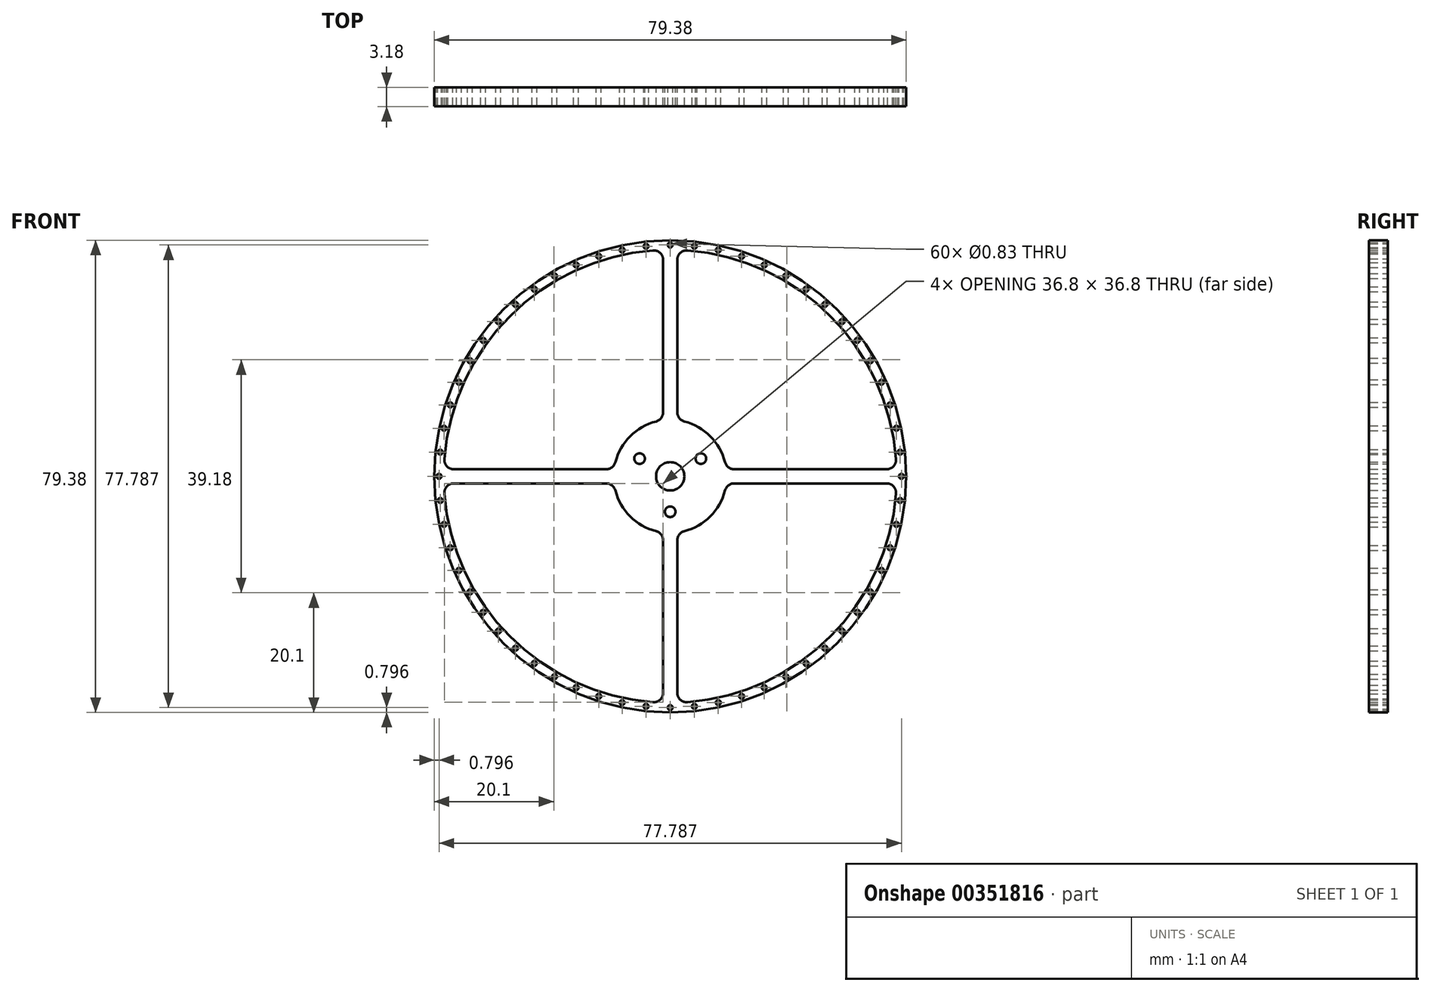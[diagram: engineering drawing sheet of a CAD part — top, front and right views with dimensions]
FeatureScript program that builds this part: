
annotation { "Feature Type Name" : "Feature", "Feature Type Description" : "" }
export const myFeature = defineFeature(function(context is Context, id is Id, definition is map)
    precondition{}
    {
        {
            var Q0;
            Q0=qCreatedBy(makeId("Front.planeOp"),FACE);
            var sketch = newSketch(context, id + "F0", { "sketchPlane" : qUnion([Q0])});
            skCircle(sketch, "E0", {"center": v(0, 0) * mm, "radius": 39.69 * mm});
            skArc(sketch, "E1", {"start": v(-0.98, 38.88) * mm, "mid": v(0.93, -38.88) * mm, "end": v(-0.88, 38.88) * mm, "construction": true});
            skArc(sketch, "E2", {"start": v(-2.9, 37.99) * mm, "mid": v(-26.94, 26.94) * mm, "end": v(-37.99, 2.9) * mm});
            skArc(sketch, "E3", {"start": v(-2.38, 9.22) * mm, "mid": v(-6.74, 6.74) * mm, "end": v(-9.22, 2.38) * mm});
            skCircle(sketch, "E4", {"center": v(0, 0) * mm, "radius": 2.38 * mm});
            skLineSegment(sketch, "E5.trimOffspring", {"start": v(1.2, 36.4) * mm, "end": v(1.2, 10.76) * mm});
            skLineSegment(sketch, "E6.trimOffspring", {"start": v(-1.2, 36.4) * mm, "end": v(-1.2, 10.76) * mm});
            skLineSegment(sketch, "E7.1.0", {"start": v(-36.4, -1.2) * mm, "end": v(-10.76, -1.2) * mm});
            skLineSegment(sketch, "E7.1.1", {"start": v(-36.4, 1.2) * mm, "end": v(-10.76, 1.2) * mm});
            skLineSegment(sketch, "E7.2.0", {"start": v(1.2, -36.4) * mm, "end": v(1.2, -10.76) * mm});
            skLineSegment(sketch, "E7.2.1", {"start": v(-1.2, -36.4) * mm, "end": v(-1.2, -10.76) * mm});
            skLineSegment(sketch, "E7.3.0", {"start": v(36.4, 1.2) * mm, "end": v(10.76, 1.2) * mm});
            skLineSegment(sketch, "E7.3.1", {"start": v(36.4, -1.2) * mm, "end": v(10.76, -1.2) * mm});
            skArc(sketch, "E8.trimOffspring", {"start": v(-9.22, -2.38) * mm, "mid": v(-6.74, -6.74) * mm, "end": v(-2.38, -9.22) * mm});
            skArc(sketch, "E9.trimOffspring", {"start": v(2.38, -9.22) * mm, "mid": v(6.74, -6.74) * mm, "end": v(9.22, -2.38) * mm});
            skArc(sketch, "E10.trimOffspring", {"start": v(9.22, 2.38) * mm, "mid": v(6.74, 6.74) * mm, "end": v(2.38, 9.22) * mm});
            skArc(sketch, "E11.trimOffspring", {"start": v(-37.99, -2.9) * mm, "mid": v(-26.94, -26.94) * mm, "end": v(-2.9, -37.99) * mm});
            skArc(sketch, "E12.trimOffspring", {"start": v(37.99, 2.9) * mm, "mid": v(26.94, 26.94) * mm, "end": v(2.9, 37.99) * mm});
            skArc(sketch, "E13.trimOffspring", {"start": v(2.9, -37.99) * mm, "mid": v(26.94, -26.94) * mm, "end": v(37.99, -2.9) * mm});
            skCircle(sketch, "E14", {"center": v(0, 0) * mm, "radius": 5.95 * mm, "construction": true});
            skLineSegment(sketch, "E15", {"start": v(0, 0) * mm, "end": v(0, -12.7) * mm, "construction": true});
            skCircle(sketch, "E16", {"center": v(0, -5.95) * mm, "radius": 0.89 * mm});
            skCircle(sketch, "E17.1.0", {"center": v(5.16, 2.98) * mm, "radius": 0.89 * mm});
            skCircle(sketch, "E17.2.0", {"center": v(-5.16, 2.98) * mm, "radius": 0.89 * mm});
            skPoint(sketch, "E18.visualSharp", {"position": v(9.45, -1.2) * mm});
            skArc(sketch, "E18.filletArc", {"start": v(10.76, -1.2) * mm, "mid": v(9.79, -1.52) * mm, "end": v(9.22, -2.38) * mm});
            skPoint(sketch, "E19.visualSharp", {"position": v(9.45, 1.2) * mm});
            skArc(sketch, "E19.filletArc", {"start": v(9.22, 2.38) * mm, "mid": v(9.79, 1.52) * mm, "end": v(10.76, 1.2) * mm});
            skPoint(sketch, "E20.visualSharp", {"position": v(1.2, -9.45) * mm});
            skArc(sketch, "E20.filletArc", {"start": v(2.38, -9.22) * mm, "mid": v(1.52, -9.79) * mm, "end": v(1.2, -10.76) * mm});
            skPoint(sketch, "E21.visualSharp", {"position": v(-1.2, -9.45) * mm});
            skArc(sketch, "E21.filletArc", {"start": v(-1.2, -10.76) * mm, "mid": v(-1.52, -9.79) * mm, "end": v(-2.38, -9.22) * mm});
            skPoint(sketch, "E22.visualSharp", {"position": v(-9.45, -1.2) * mm});
            skArc(sketch, "E22.filletArc", {"start": v(-9.22, -2.38) * mm, "mid": v(-9.79, -1.52) * mm, "end": v(-10.76, -1.2) * mm});
            skPoint(sketch, "E23.visualSharp", {"position": v(-9.45, 1.2) * mm});
            skArc(sketch, "E23.filletArc", {"start": v(-10.76, 1.2) * mm, "mid": v(-9.79, 1.52) * mm, "end": v(-9.22, 2.38) * mm});
            skPoint(sketch, "E24.visualSharp", {"position": v(-1.2, 9.45) * mm});
            skArc(sketch, "E24.filletArc", {"start": v(-2.38, 9.22) * mm, "mid": v(-1.52, 9.79) * mm, "end": v(-1.2, 10.76) * mm});
            skPoint(sketch, "E25.visualSharp", {"position": v(1.2, 9.45) * mm});
            skArc(sketch, "E25.filletArc", {"start": v(1.2, 10.76) * mm, "mid": v(1.52, 9.79) * mm, "end": v(2.38, 9.22) * mm});
            skPoint(sketch, "E26.visualSharp", {"position": v(38.08, 1.2) * mm});
            skArc(sketch, "E26.filletArc", {"start": v(36.4, 1.2) * mm, "mid": v(37.57, 1.7) * mm, "end": v(37.99, 2.9) * mm});
            skPoint(sketch, "E27.visualSharp", {"position": v(38.08, -1.2) * mm});
            skArc(sketch, "E27.filletArc", {"start": v(37.99, -2.9) * mm, "mid": v(37.57, -1.7) * mm, "end": v(36.4, -1.2) * mm});
            skPoint(sketch, "E28.visualSharp", {"position": v(1.2, -38.08) * mm});
            skArc(sketch, "E28.filletArc", {"start": v(1.2, -36.4) * mm, "mid": v(1.7, -37.57) * mm, "end": v(2.9, -37.99) * mm});
            skPoint(sketch, "E29.visualSharp", {"position": v(-1.2, -38.08) * mm});
            skArc(sketch, "E29.filletArc", {"start": v(-2.9, -37.99) * mm, "mid": v(-1.7, -37.57) * mm, "end": v(-1.2, -36.4) * mm});
            skPoint(sketch, "E30.visualSharp", {"position": v(-38.08, -1.2) * mm});
            skArc(sketch, "E30.filletArc", {"start": v(-36.4, -1.2) * mm, "mid": v(-37.57, -1.7) * mm, "end": v(-37.99, -2.9) * mm});
            skPoint(sketch, "E31.visualSharp", {"position": v(-38.08, 1.2) * mm});
            skArc(sketch, "E31.filletArc", {"start": v(-37.99, 2.9) * mm, "mid": v(-37.57, 1.7) * mm, "end": v(-36.4, 1.2) * mm});
            skPoint(sketch, "E32.visualSharp", {"position": v(-1.2, 38.08) * mm});
            skArc(sketch, "E32.filletArc", {"start": v(-1.2, 36.4) * mm, "mid": v(-1.7, 37.57) * mm, "end": v(-2.9, 37.99) * mm});
            skPoint(sketch, "E33.visualSharp", {"position": v(1.2, 38.08) * mm});
            skArc(sketch, "E33.filletArc", {"start": v(2.9, 37.99) * mm, "mid": v(1.7, 37.57) * mm, "end": v(1.2, 36.4) * mm});
            skLineSegment(sketch, "E34", {"start": v(0, 0) * mm, "end": v(-43.18, 0) * mm, "construction": true});
            skCircle(sketch, "E35", {"center": v(-38.9, 0) * mm, "radius": 0.41 * mm});
            skCircle(sketch, "E36.1.0", {"center": v(-38.68, -4.07) * mm, "radius": 0.41 * mm});
            skCircle(sketch, "E36.2.0", {"center": v(-38.04, -8.09) * mm, "radius": 0.41 * mm});
            skCircle(sketch, "E36.3.0", {"center": v(-37, -12.02) * mm, "radius": 0.41 * mm});
            skCircle(sketch, "E36.4.0", {"center": v(-35.53, -15.82) * mm, "radius": 0.41 * mm});
            skCircle(sketch, "E36.5.0", {"center": v(-33.68, -19.45) * mm, "radius": 0.41 * mm});
            skCircle(sketch, "E36.6.0", {"center": v(-31.47, -22.86) * mm, "radius": 0.41 * mm});
            skCircle(sketch, "E36.7.0", {"center": v(-28.9, -26.02) * mm, "radius": 0.41 * mm});
            skCircle(sketch, "E36.8.0", {"center": v(-26.02, -28.9) * mm, "radius": 0.41 * mm});
            skCircle(sketch, "E36.9.0", {"center": v(-22.86, -31.47) * mm, "radius": 0.41 * mm});
            skCircle(sketch, "E36.10.0", {"center": v(-19.45, -33.68) * mm, "radius": 0.41 * mm});
            skCircle(sketch, "E36.11.0", {"center": v(-15.82, -35.53) * mm, "radius": 0.41 * mm});
            skCircle(sketch, "E36.12.0", {"center": v(-12.02, -37) * mm, "radius": 0.41 * mm});
            skCircle(sketch, "E36.13.0", {"center": v(-8.09, -38.04) * mm, "radius": 0.41 * mm});
            skCircle(sketch, "E36.14.0", {"center": v(-4.07, -38.68) * mm, "radius": 0.41 * mm});
            skCircle(sketch, "E36.15.0", {"center": v(0, -38.9) * mm, "radius": 0.41 * mm});
            skCircle(sketch, "E36.16.0", {"center": v(4.07, -38.68) * mm, "radius": 0.41 * mm});
            skCircle(sketch, "E36.17.0", {"center": v(8.09, -38.04) * mm, "radius": 0.41 * mm});
            skCircle(sketch, "E36.18.0", {"center": v(12.02, -37) * mm, "radius": 0.41 * mm});
            skCircle(sketch, "E36.19.0", {"center": v(15.82, -35.53) * mm, "radius": 0.41 * mm});
            skCircle(sketch, "E36.20.0", {"center": v(19.45, -33.68) * mm, "radius": 0.41 * mm});
            skCircle(sketch, "E36.21.0", {"center": v(22.86, -31.47) * mm, "radius": 0.41 * mm});
            skCircle(sketch, "E36.22.0", {"center": v(26.02, -28.9) * mm, "radius": 0.41 * mm});
            skCircle(sketch, "E36.23.0", {"center": v(28.9, -26.02) * mm, "radius": 0.41 * mm});
            skCircle(sketch, "E36.24.0", {"center": v(31.47, -22.86) * mm, "radius": 0.41 * mm});
            skCircle(sketch, "E36.25.0", {"center": v(33.68, -19.45) * mm, "radius": 0.41 * mm});
            skCircle(sketch, "E36.26.0", {"center": v(35.53, -15.82) * mm, "radius": 0.41 * mm});
            skCircle(sketch, "E36.27.0", {"center": v(37, -12.02) * mm, "radius": 0.41 * mm});
            skCircle(sketch, "E36.28.0", {"center": v(38.04, -8.09) * mm, "radius": 0.41 * mm});
            skCircle(sketch, "E36.29.0", {"center": v(38.68, -4.07) * mm, "radius": 0.41 * mm});
            skCircle(sketch, "E36.30.0", {"center": v(38.9, 0) * mm, "radius": 0.41 * mm});
            skCircle(sketch, "E36.31.0", {"center": v(38.68, 4.07) * mm, "radius": 0.41 * mm});
            skCircle(sketch, "E36.32.0", {"center": v(38.04, 8.09) * mm, "radius": 0.41 * mm});
            skCircle(sketch, "E36.33.0", {"center": v(37, 12.02) * mm, "radius": 0.41 * mm});
            skCircle(sketch, "E36.34.0", {"center": v(35.53, 15.82) * mm, "radius": 0.41 * mm});
            skCircle(sketch, "E36.35.0", {"center": v(33.68, 19.45) * mm, "radius": 0.41 * mm});
            skCircle(sketch, "E36.36.0", {"center": v(31.47, 22.86) * mm, "radius": 0.41 * mm});
            skCircle(sketch, "E36.37.0", {"center": v(28.9, 26.02) * mm, "radius": 0.41 * mm});
            skCircle(sketch, "E36.38.0", {"center": v(26.02, 28.9) * mm, "radius": 0.41 * mm});
            skCircle(sketch, "E36.39.0", {"center": v(22.86, 31.47) * mm, "radius": 0.41 * mm});
            skCircle(sketch, "E36.40.0", {"center": v(19.45, 33.68) * mm, "radius": 0.41 * mm});
            skCircle(sketch, "E36.41.0", {"center": v(15.82, 35.53) * mm, "radius": 0.41 * mm});
            skCircle(sketch, "E36.42.0", {"center": v(12.02, 37) * mm, "radius": 0.41 * mm});
            skCircle(sketch, "E36.43.0", {"center": v(8.09, 38.04) * mm, "radius": 0.41 * mm});
            skCircle(sketch, "E36.44.0", {"center": v(4.07, 38.68) * mm, "radius": 0.41 * mm});
            skCircle(sketch, "E36.45.0", {"center": v(0, 38.9) * mm, "radius": 0.41 * mm});
            skCircle(sketch, "E36.46.0", {"center": v(-4.07, 38.68) * mm, "radius": 0.41 * mm});
            skCircle(sketch, "E36.47.0", {"center": v(-8.09, 38.04) * mm, "radius": 0.41 * mm});
            skCircle(sketch, "E36.48.0", {"center": v(-12.02, 37) * mm, "radius": 0.41 * mm});
            skCircle(sketch, "E36.49.0", {"center": v(-15.82, 35.53) * mm, "radius": 0.41 * mm});
            skCircle(sketch, "E36.50.0", {"center": v(-19.45, 33.68) * mm, "radius": 0.41 * mm});
            skCircle(sketch, "E36.51.0", {"center": v(-22.86, 31.47) * mm, "radius": 0.41 * mm});
            skCircle(sketch, "E36.52.0", {"center": v(-26.02, 28.9) * mm, "radius": 0.41 * mm});
            skCircle(sketch, "E36.53.0", {"center": v(-28.9, 26.02) * mm, "radius": 0.41 * mm});
            skCircle(sketch, "E36.54.0", {"center": v(-31.47, 22.86) * mm, "radius": 0.41 * mm});
            skCircle(sketch, "E36.55.0", {"center": v(-33.68, 19.45) * mm, "radius": 0.41 * mm});
            skCircle(sketch, "E36.56.0", {"center": v(-35.53, 15.82) * mm, "radius": 0.41 * mm});
            skCircle(sketch, "E36.57.0", {"center": v(-37, 12.02) * mm, "radius": 0.41 * mm});
            skCircle(sketch, "E36.58.0", {"center": v(-38.04, 8.09) * mm, "radius": 0.41 * mm});
            skCircle(sketch, "E36.59.0", {"center": v(-38.68, 4.07) * mm, "radius": 0.41 * mm});
            skSolve(sketch);
        }
        {
            var Q0;
            Q0=makeQuery(id+"F0.imprint","IMPRINT",FACE,{"disambiguationData":[TD([[makeQuery(id+"F0.imprint","IMPRINT",EDGE,{"derivedFrom":sQuery(id+"F0.wireOp",EDGE,"E0")}),1.0]])]});
            extrude(context, id + "F1", {"entities" : qUnion([Q0]), "depth" : 3.17 * mm});
        }
    });
